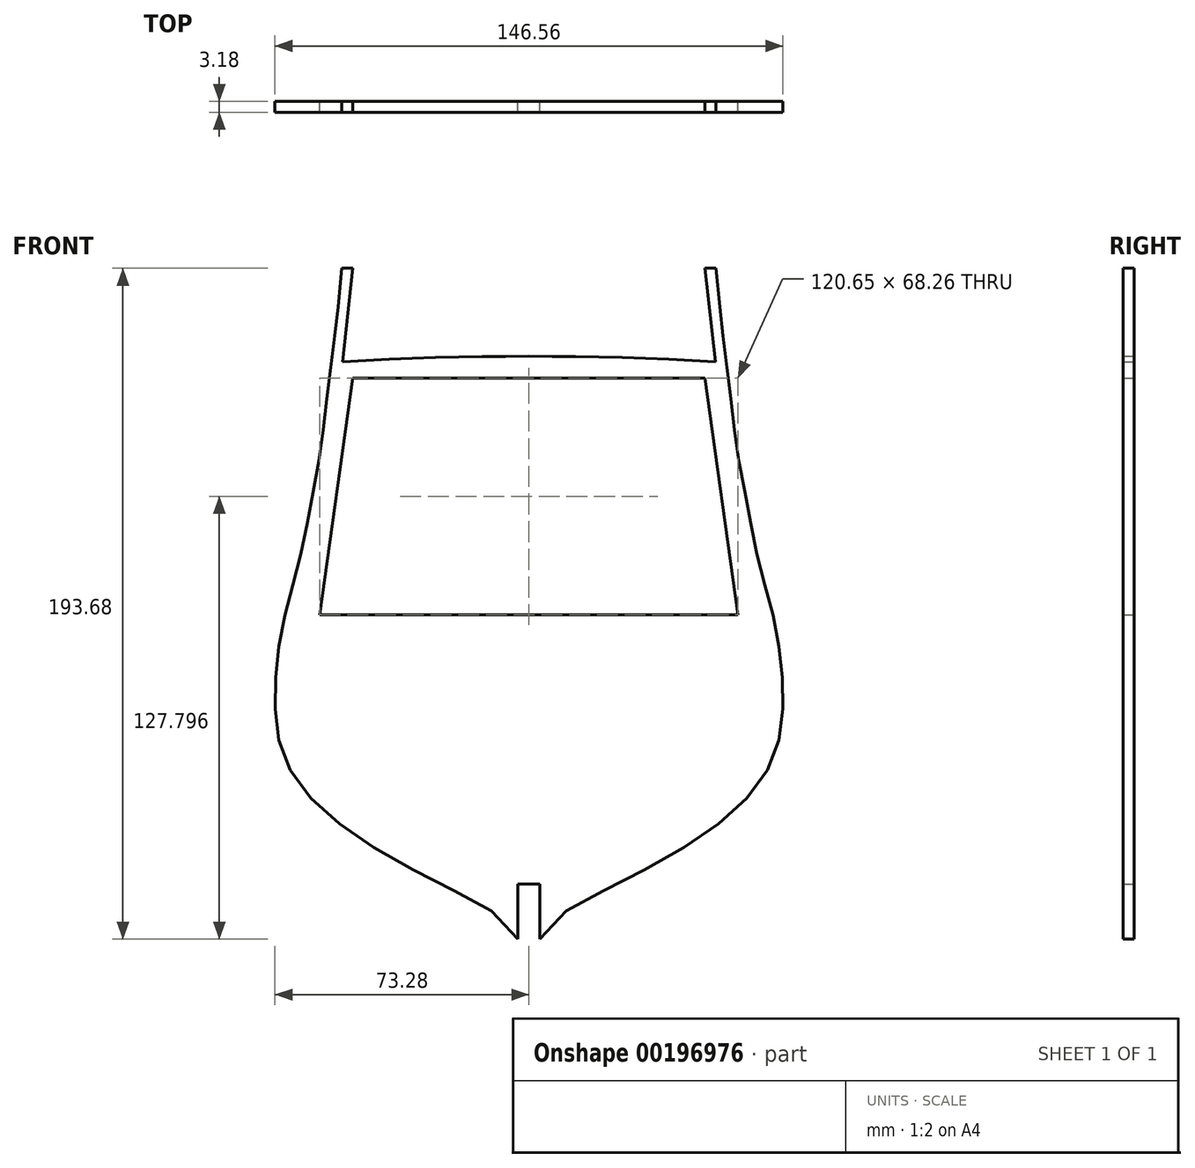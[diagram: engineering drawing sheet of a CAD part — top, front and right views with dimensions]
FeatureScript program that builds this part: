
annotation { "Feature Type Name" : "Feature", "Feature Type Description" : "" }
export const myFeature = defineFeature(function(context is Context, id is Id, definition is map)
    precondition{}
    {
        {
            var Q0;
            Q0=qCreatedBy(makeId("Front.planeOp"),FACE);
            var sketch = newSketch(context, id + "F0", { "sketchPlane" : qUnion([Q0])});
            skLineSegment(sketch, "E0.bottom", {"start": v(76.2, 96.84) * mm, "end": v(-76.2, 96.84) * mm, "construction": true});
            skLineSegment(sketch, "E0.top", {"start": v(76.2, -96.84) * mm, "end": v(-76.2, -96.84) * mm, "construction": true});
            skLineSegment(sketch, "E0.left", {"start": v(76.2, 96.84) * mm, "end": v(76.2, -96.84) * mm, "construction": true});
            skLineSegment(sketch, "E0.right", {"start": v(-76.2, 96.84) * mm, "end": v(-76.2, -96.84) * mm, "construction": true});
            skPoint(sketch, "E0.middle", {"position": v(0, 0) * mm});
            skLineSegment(sketch, "E1", {"start": v(-3.17, -96.84) * mm, "end": v(-3.17, -80.96) * mm});
            skLineSegment(sketch, "E2", {"start": v(-3.17, -80.96) * mm, "end": v(0, -80.96) * mm});
            skLineSegment(sketch, "E3", {"start": v(0, -80.96) * mm, "end": v(3.18, -80.96) * mm});
            skLineSegment(sketch, "E4", {"start": v(3.17, -80.96) * mm, "end": v(3.17, -96.84) * mm});
            skLineSegment(sketch, "E5", {"start": v(0, -3.17) * mm, "end": v(-60.33, -3.17) * mm});
            skLineSegment(sketch, "E6", {"start": v(-60.33, -3.17) * mm, "end": v(-50.8, 65.09) * mm});
            skLineSegment(sketch, "E7", {"start": v(-50.8, 65.09) * mm, "end": v(0, 65.09) * mm});
            skLineSegment(sketch, "E8", {"start": v(0, 65.09) * mm, "end": v(50.8, 65.09) * mm});
            skLineSegment(sketch, "E9", {"start": v(50.8, 65.09) * mm, "end": v(60.33, -3.17) * mm});
            skLineSegment(sketch, "E10", {"start": v(60.33, -3.17) * mm, "end": v(0, -3.17) * mm});
            skFitSpline(sketch, "E11", {"points": [v(3.17, -96.84) * mm, v(19.05, -84.14) * mm, v(42.86, -71.44) * mm, v(60.33, -58.74) * mm, v(69.85, -46.04) * mm, v(73.03, -33.34) * mm, v(73.03, -20.64) * mm, v(71.44, -7.94) * mm, v(68.26, 4.76) * mm, v(65.09, 17.46) * mm, v(62.7, 30.16) * mm, v(60.33, 42.86) * mm, v(58.74, 55.56) * mm, v(57.15, 68.26) * mm, v(55.56, 80.96) * mm, v(53.98, 96.84) * mm], "startDerivative": vector(123.05, 246.1) * mm, "endDerivative": vector(-34.73, 347.29) * mm});
            skLineSegment(sketch, "E12", {"start": v(0, -96.84) * mm, "end": v(0, 96.84) * mm, "construction": true});
            skLineSegment(sketch, "E13", {"start": v(53.98, 96.84) * mm, "end": v(50.8, 96.84) * mm});
            skLineSegment(sketch, "E14", {"start": v(50.8, 96.84) * mm, "end": v(53.77, 69.85) * mm});
            skPoint(sketch, "E15", {"position": v(0, 71.44) * mm});
            skLineSegment(sketch, "E16", {"start": v(53.77, 69.85) * mm, "end": v(56.94, 69.85) * mm, "construction": true});
            skLineSegment(sketch, "E17.MirrorCS", {"start": v(-50.8, 96.84) * mm, "end": v(-53.77, 69.85) * mm});
            skLineSegment(sketch, "E18.MirrorCS", {"start": v(-53.98, 96.84) * mm, "end": v(-50.8, 96.84) * mm});
            skFitSpline(sketch, "E19.MirrorCS", {"points": [v(-3.18, -96.84) * mm, v(-19.05, -84.14) * mm, v(-42.86, -71.44) * mm, v(-60.33, -58.74) * mm, v(-69.85, -46.04) * mm, v(-73.03, -33.34) * mm, v(-73.03, -20.64) * mm, v(-71.44, -7.94) * mm, v(-68.26, 4.76) * mm, v(-65.09, 17.46) * mm, v(-62.7, 30.16) * mm, v(-60.33, 42.86) * mm, v(-58.74, 55.56) * mm, v(-57.15, 68.26) * mm, v(-55.56, 80.96) * mm, v(-53.98, 96.84) * mm], "startDerivative": vector(-123.05, 246.1) * mm, "endDerivative": vector(34.73, 347.29) * mm});
            skArc(sketch, "E20", {"start": v(53.77, 69.85) * mm, "mid": v(0, 71.44) * mm, "end": v(-53.77, 69.85) * mm});
            skSolve(sketch);
        }
        {
            var Q0;
            Q0=makeQuery(id+"F0.imprint","IMPRINT",FACE,{"disambiguationData":[TD([[makeQuery(id+"F0.imprint","IMPRINT",EDGE,{"derivedFrom":sQuery(id+"F0.wireOp",EDGE,"E1")}),1.0]])]});
            extrude(context, id + "F1", {"entities" : qUnion([Q0]), "endBound" : BoundingType.SYMMETRIC, "depth" : 3.17 * mm});
        }
    });
